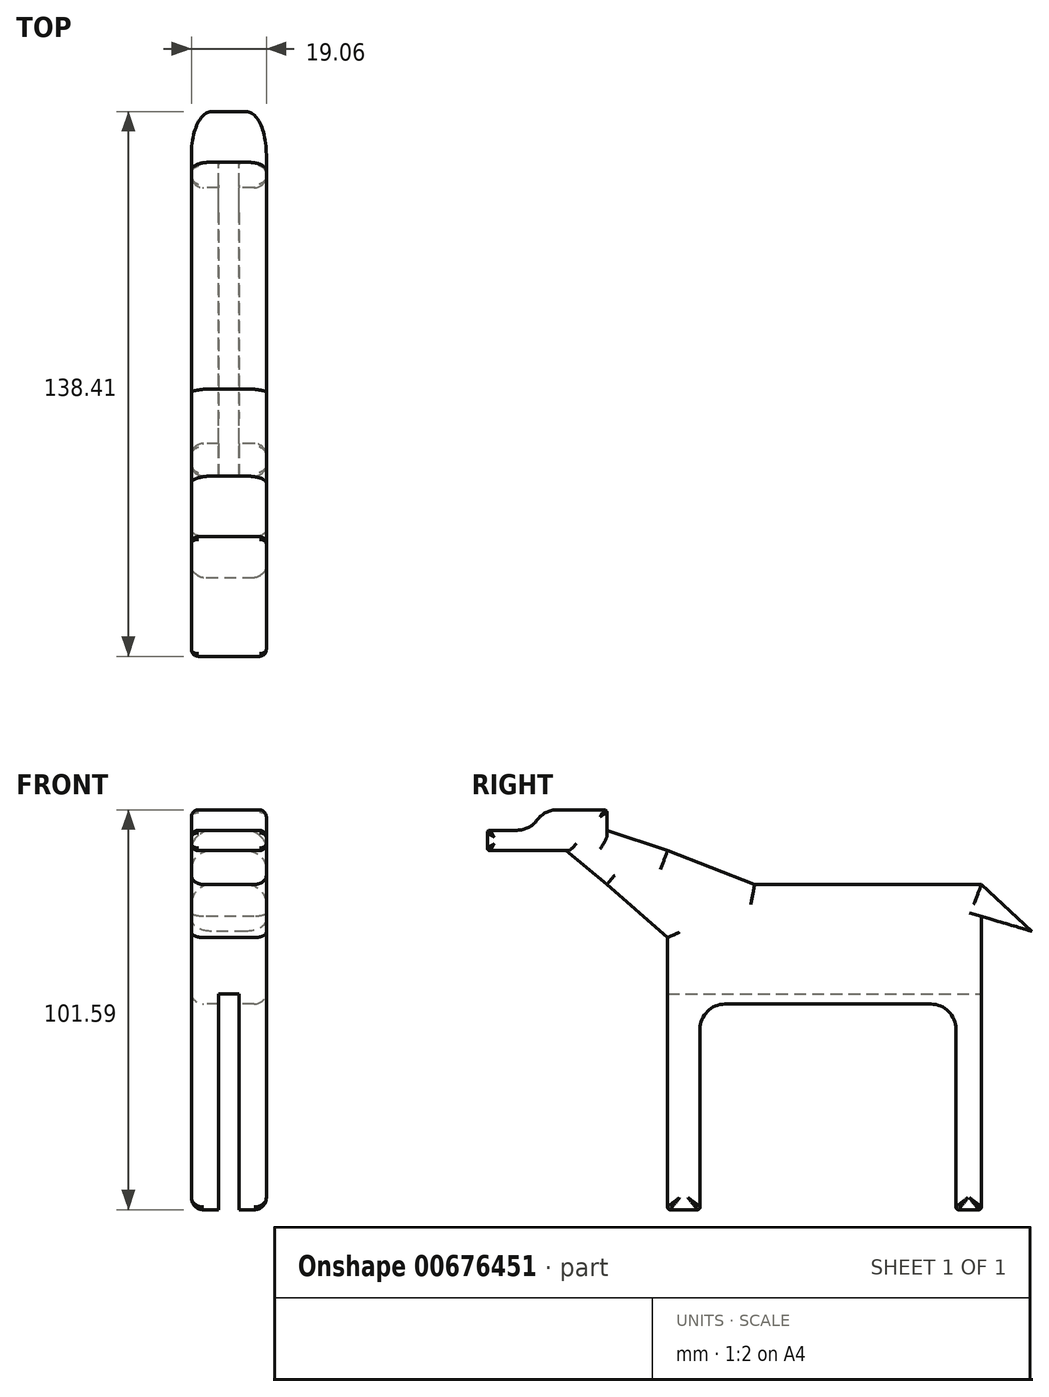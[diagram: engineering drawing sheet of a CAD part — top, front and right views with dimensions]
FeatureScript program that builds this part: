
annotation { "Feature Type Name" : "Feature", "Feature Type Description" : "" }
export const myFeature = defineFeature(function(context is Context, id is Id, definition is map)
    precondition{}
    {
        {
            var Q0;
            Q0=qCreatedBy(makeId("Right.planeOp"),FACE);
            var sketch = newSketch(context, id + "F0", { "sketchPlane" : qUnion([Q0])});
            skLineSegment(sketch, "E0.bottom", {"start": v(-4.86, 41.49) * mm, "end": v(52.78, 41.49) * mm});
            skLineSegment(sketch, "E0.top", {"start": v(-12.35, 11.08) * mm, "end": v(39.94, 11.08) * mm});
            skLineSegment(sketch, "E0.left", {"start": v(-26.99, 27.97) * mm, "end": v(-26.99, 11.08) * mm});
            skLineSegment(sketch, "E0.right", {"start": v(52.78, 33.37) * mm, "end": v(52.78, 11.08) * mm});
            skLineSegment(sketch, "E1.bottom", {"start": v(-52.82, 50.07) * mm, "end": v(-61.33, 50.07) * mm});
            skLineSegment(sketch, "E1.top", {"start": v(-43.05, 60.45) * mm, "end": v(-54.98, 60.45) * mm});
            skLineSegment(sketch, "E1.left", {"start": v(-42.37, 55.26) * mm, "end": v(-42.37, 59.77) * mm});
            skLineSegment(sketch, "E2.bottom", {"start": v(-61.33, 50.07) * mm, "end": v(-72.1, 50.07) * mm});
            skLineSegment(sketch, "E2.top", {"start": v(-65.21, 55.26) * mm, "end": v(-72.1, 55.26) * mm});
            skLineSegment(sketch, "E2.right", {"start": v(-72.77, 50.75) * mm, "end": v(-72.77, 54.58) * mm});
            skLineSegment(sketch, "E3.top", {"start": v(-26.3, -41.14) * mm, "end": v(-19.39, -41.14) * mm});
            skLineSegment(sketch, "E3.left", {"start": v(-26.99, 11.08) * mm, "end": v(-26.99, -40.46) * mm});
            skLineSegment(sketch, "E3.right", {"start": v(-18.7, 4.73) * mm, "end": v(-18.7, -40.46) * mm});
            skLineSegment(sketch, "E4.top", {"start": v(52.1, -41.14) * mm, "end": v(46.97, -41.14) * mm});
            skLineSegment(sketch, "E4.left", {"start": v(52.78, 11.08) * mm, "end": v(52.78, -40.46) * mm});
            skLineSegment(sketch, "E4.right", {"start": v(46.29, 4.73) * mm, "end": v(46.29, -40.46) * mm});
            skLineSegment(sketch, "E5", {"start": v(-42.37, 55.26) * mm, "end": v(-26.99, 50.07) * mm});
            skLineSegment(sketch, "E6", {"start": v(-26.99, 50.07) * mm, "end": v(-4.86, 41.49) * mm});
            skLineSegment(sketch, "E7", {"start": v(-52.82, 50.07) * mm, "end": v(-42.37, 41.49) * mm});
            skLineSegment(sketch, "E8", {"start": v(-42.37, 41.49) * mm, "end": v(-26.99, 27.97) * mm});
            skArc(sketch, "E9.filletArc", {"start": v(-54.98, 60.45) * mm, "mid": v(-57.84, 59.76) * mm, "end": v(-60.1, 57.85) * mm});
            skArc(sketch, "E10.filletArc", {"start": v(-65.21, 55.26) * mm, "mid": v(-62.35, 55.95) * mm, "end": v(-60.1, 57.85) * mm});
            skArc(sketch, "E11.filletArc", {"start": v(-72.1, 55.26) * mm, "mid": v(-72.57, 55.06) * mm, "end": v(-72.77, 54.58) * mm});
            skArc(sketch, "E12.filletArc", {"start": v(-72.77, 50.75) * mm, "mid": v(-72.57, 50.27) * mm, "end": v(-72.1, 50.07) * mm});
            skArc(sketch, "E13.filletArc", {"start": v(-42.37, 59.77) * mm, "mid": v(-42.57, 60.25) * mm, "end": v(-43.05, 60.45) * mm});
            skArc(sketch, "E14.filletArc", {"start": v(-12.35, 11.08) * mm, "mid": v(-16.84, 9.22) * mm, "end": v(-18.7, 4.73) * mm});
            skArc(sketch, "E15.filletArc", {"start": v(46.29, 4.73) * mm, "mid": v(44.43, 9.22) * mm, "end": v(39.94, 11.08) * mm});
            skArc(sketch, "E16.filletArc", {"start": v(-19.39, -41.14) * mm, "mid": v(-18.9, -40.94) * mm, "end": v(-18.7, -40.46) * mm});
            skArc(sketch, "E17.filletArc", {"start": v(-26.99, -40.46) * mm, "mid": v(-26.79, -40.94) * mm, "end": v(-26.3, -41.14) * mm});
            skArc(sketch, "E18.filletArc", {"start": v(46.29, -40.46) * mm, "mid": v(46.49, -40.94) * mm, "end": v(46.97, -41.14) * mm});
            skArc(sketch, "E19.filletArc", {"start": v(52.1, -41.14) * mm, "mid": v(52.58, -40.94) * mm, "end": v(52.78, -40.46) * mm});
            skLineSegment(sketch, "E20", {"start": v(52.78, 33.37) * mm, "end": v(65.64, 29.59) * mm});
            skLineSegment(sketch, "E21", {"start": v(65.64, 29.59) * mm, "end": v(52.78, 41.49) * mm});
            skSolve(sketch);
        }
        {
            var Q0;
            Q0=makeQuery(id+"F0.imprint","IMPRINT",FACE,{"disambiguationData":[TD([[makeQuery(id+"F0.imprint","IMPRINT",EDGE,{"derivedFrom":sQuery(id+"F0.wireOp",EDGE,"E0.bottom")}),-1.0]])]});
            extrude(context, id + "F1", {"entities" : qUnion([Q0]), "endBound" : BoundingType.SYMMETRIC, "depth" : 19.05 * mm, "offsetDistance" : 25.4 * mm});
        }
        {
            var Q0;
            Q0=makeQuery(id+"F1.opExtrude","CAP_EDGE",EDGE,{"disambiguationData":[OSD([sQuery(id+"F0.wireOp",EDGE,"E0.bottom")])],"isStart":false});
            var Q1;
            Q1=makeQuery(id+"F1.opExtrude","CAP_EDGE",EDGE,{"disambiguationData":[OSD([sQuery(id+"F0.wireOp",EDGE,"E6")])],"isStart":false});
            var Q2;
            Q2=makeQuery(id+"F1.opExtrude","CAP_EDGE",EDGE,{"disambiguationData":[OSD([sQuery(id+"F0.wireOp",EDGE,"E5")])],"isStart":false});
            var Q3;
            Q3=makeQuery(id+"F1.opExtrude","CAP_EDGE",EDGE,{"disambiguationData":[OSD([sQuery(id+"F0.wireOp",EDGE,"E0.bottom")])],"isStart":true});
            var Q4;
            Q4=makeQuery(id+"F1.opExtrude","CAP_EDGE",EDGE,{"disambiguationData":[OSD([sQuery(id+"F0.wireOp",EDGE,"E6")])],"isStart":true});
            var Q5;
            Q5=makeQuery(id+"F1.opExtrude","CAP_EDGE",EDGE,{"disambiguationData":[OSD([sQuery(id+"F0.wireOp",EDGE,"E5")])],"isStart":true});
            var Q6;
            Q6=makeQuery(id+"F1.opExtrude","CAP_EDGE",EDGE,{"disambiguationData":[OSD([sQuery(id+"F0.wireOp",EDGE,"E21")])],"isStart":true});
            var Q7;
            Q7=makeQuery(id+"F1.opExtrude","CAP_EDGE",EDGE,{"disambiguationData":[OSD([sQuery(id+"F0.wireOp",EDGE,"E21")])],"isStart":false});
            fillet(context, id + "F2", {"entities" : qUnion([Q0, Q1, Q2, Q3, Q4, Q5, Q6, Q7]), "radius" : 5.08 * mm, "tangentPropagation" : true, "allowEdgeOverflow" : false});
        }
        {
            var Q0;
            Q0=makeQuery(id+"F1.opExtrude","CAP_EDGE",EDGE,{"disambiguationData":[OSD([sQuery(id+"F0.wireOp",EDGE,"E1.left")])],"isStart":true});
            var Q1;
            Q1=makeQuery(id+"F1.opExtrude","CAP_EDGE",EDGE,{"disambiguationData":[OSD([sQuery(id+"F0.wireOp",EDGE,"E1.top")])],"isStart":true});
            var Q2;
            Q2=makeQuery(id+"F1.opExtrude","CAP_EDGE",EDGE,{"disambiguationData":[OSD([sQuery(id+"F0.wireOp",EDGE,"E1.top")])],"isStart":false});
            var Q3;
            Q3=makeQuery(id+"F1.opExtrude","CAP_EDGE",EDGE,{"disambiguationData":[OSD([sQuery(id+"F0.wireOp",EDGE,"E1.left")])],"isStart":false});
            fillet(context, id + "F3", {"entities" : qUnion([Q0, Q1, Q2, Q3]), "radius" : 1.78 * mm, "tangentPropagation" : true, "allowEdgeOverflow" : false});
        }
        {
            var Q0;
            Q0=makeQuery(id+"F1.opExtrude","CAP_EDGE",EDGE,{"disambiguationData":[OSD([sQuery(id+"F0.wireOp",EDGE,"E7")])],"isStart":false});
            var Q1;
            Q1=makeQuery(id+"F1.opExtrude","CAP_EDGE",EDGE,{"disambiguationData":[OSD([sQuery(id+"F0.wireOp",EDGE,"E8")])],"isStart":false});
            var Q2;
            Q2=makeQuery(id+"F1.opExtrude","CAP_EDGE",EDGE,{"disambiguationData":[OSD([sQuery(id+"F0.wireOp",EDGE,"E8")])],"isStart":true});
            var Q3;
            Q3=makeQuery(id+"F1.opExtrude","CAP_EDGE",EDGE,{"disambiguationData":[OSD([sQuery(id+"F0.wireOp",EDGE,"E7")])],"isStart":true});
            var Q4;
            Q4=makeQuery(id+"F1.opExtrude","CAP_EDGE",EDGE,{"disambiguationData":[OSD([sQuery(id+"F0.wireOp",EDGE,"E0.left"),sQuery(id+"F0.wireOp",EDGE,"E3.left")])],"isStart":true});
            var Q5;
            Q5=makeQuery(id+"F1.opExtrude","CAP_EDGE",EDGE,{"disambiguationData":[OSD([sQuery(id+"F0.wireOp",EDGE,"E0.left"),sQuery(id+"F0.wireOp",EDGE,"E3.left")])],"isStart":false});
            fillet(context, id + "F4", {"entities" : qUnion([Q0, Q1, Q2, Q3, Q4, Q5]), "radius" : 3.07 * mm, "tangentPropagation" : true, "allowEdgeOverflow" : false});
        }
        {
            var Q0;
            Q0=qCreatedBy(makeId("Front.planeOp"),FACE);
            var sketch = newSketch(context, id + "F5", { "sketchPlane" : qUnion([Q0])});
            skLineSegment(sketch, "E22.bottom", {"start": v(-2.56, -42.56) * mm, "end": v(0, -42.56) * mm});
            skLineSegment(sketch, "E22.top", {"start": v(-2.56, 13.69) * mm, "end": v(0, 13.69) * mm});
            skLineSegment(sketch, "E22.left", {"start": v(-2.56, -42.56) * mm, "end": v(-2.56, 13.69) * mm});
            skLineSegment(sketch, "E23.MirrorCS", {"start": v(2.56, -42.56) * mm, "end": v(0, -42.56) * mm});
            skLineSegment(sketch, "E24.MirrorCS", {"start": v(2.56, 13.69) * mm, "end": v(0, 13.69) * mm});
            skLineSegment(sketch, "E25.MirrorCS", {"start": v(2.56, -42.56) * mm, "end": v(2.56, 13.69) * mm});
            skSolve(sketch);
        }
        {
            var Q0;
            Q0=makeQuery(id+"F5.imprint","IMPRINT",FACE,{"disambiguationData":[TD([[makeQuery(id+"F5.imprint","IMPRINT",EDGE,{"derivedFrom":sQuery(id+"F5.wireOp",EDGE,"E22.bottom")}),1.0]])]});
            extrude(context, id + "F6", {"entities" : qUnion([Q0]), "operationType" : NewBodyOperationType.REMOVE, "depth" : 44.45 * mm, "offsetDistance" : 25.4 * mm, "hasSecondDirection" : true, "secondDirectionOppositeDirection" : true, "secondDirectionDepth" : 66.04 * mm});
        }
    });
